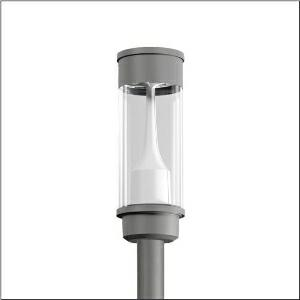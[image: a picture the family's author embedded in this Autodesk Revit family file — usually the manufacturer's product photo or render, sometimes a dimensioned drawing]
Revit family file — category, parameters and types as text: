
# Revit family: litepole_iq___p1_0a_5xa5415ff14hp_e299
name_source: partatom
category: Lighting Fixtures
units: mm (PartAtom-declared; Revit-internal decimal feet)

## family parameters
Cut with Voids When Loaded = No
Host = Face
Light Source = No
Part Type = Normal
Room Calculation Point = No
Round Connector Dimension = Use Diameter
Shared = No

## types (1)
- --- (1 x LED, 4700 lm, 33.6 W, 3000K)
    Apparent Load = 34 VA
    CIE Flux Codes = 31 60 90 94 100
    Color Rendering = 70
    Color Temperature = 3000K
    Default Elevation = 1800 mm
    Description = Litepole iQ, mast luminaire, Module 540 iQ-SR, primary light control with 3 zone facetted reflector, of plastic, silver coated, highly specular, structured, primary optical cover: cover, of PMMA, transparent, partly coated, light distribution: P1.0a, light emission: direct distribution, primary light characteristic: strongly asymmetric, installation type: post-top, LED, High Power LED, rated luminous flux: 4.700lm, luminous efficacy: 140lm/W, light colour: 730, colour temperature: 3000K, control gear: iQ Street-Remote, control: optimised constant luminous flux control (CLO 2.0), Desk-Remote (wireless, voltage-free reading and setting of iQ features in the workshop via application-optimized NFC function/RFID function), Light-Fading, Smart-Wire, Night-Set, Lumen-Switch, Temp-Guard, Auto-Match, Street-Remote, pre-setting: logarithmic dimming characteristic, with terminal, 6-pole, max. 2.5mm², mains connection: 230..240V, AC, 50/60Hz, start of lifetime: 34W, end of service life: 36W, reduction: 15W, luminaire housing, upper part, of glass-fibre reinforced polyester, coated, Siteco® metallic grey (DB 702S), diameter: 210mm, height: 590mm, spigot size: d x l = 76 x 70mm (post-top) | with reducer (optional accessory) 60 x 70mm, mounting height: 3..5m, post-top mast mounting element, of diecast aluminium, coated, Siteco® metallic grey (DB 702S), Module 540 iQ-SR, traffic white (RAL 9016), equipment: Power, protection rating (complete): IP65, insulation class (complete): insulation class II (safety insulation), certification: CE, ENEC, VDE, packaging unit: 1 piece

Light Distribution: P1.0a
    Height = 590 mm
    Lamp = 1 x LED
    Lamp Light Flux = 4700 lm
    Lamp Power = 33.6 W
    Lamp count = 1
    Length = 220 mm
    Luminous efficacy = 140 lm/W
    Manufacturer = Siteco
    ModVariant = No
    Model = 5XA5415FF14HP
    Number of Poles = 1
    OnlyDefault = Yes
    Power Factor = 1
    Product Name = Litepole iQ | P1.0a
    Product group = mast luminaire | pylon top
    ProductGroupID = 6100
    Protection Class = Protection class II
    Protection Degree = IP 65
    RLX_Detail_Level = 1
    RLX_Emergency_Light_Flux = 0 lm
    RLX_Emergency_Type = 0
    RLX_Emergency_Type_DB = No
    RlxData = <blob elided: 29949 chars, md5=31fcfad7>
    Socket = socket
    Standby Power = 0 W
    System Light Flux = 4700 lm
    System Power = 34 W
    Type Comments = factory setting: luminous flux: 100 % | dim-lin: 254 | 695 mA
    Type Image = l_1006025.jpg
    URL = http://relux.com
    VarID = @adj_216235
    Voltage = 0 V
    Weight = 0.00 kg
    Width = 0 mm  [stored 0 ft]

note: [stored X ft] marks values corroborated as IEEE doubles in the binary element streams (Revit-internal decimal feet)

## geometry (parser evidence)
native form markers: Blend x4, Sweep x12
no freeform markers — native parametric forms only
